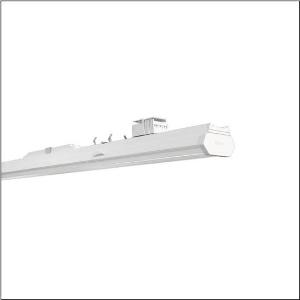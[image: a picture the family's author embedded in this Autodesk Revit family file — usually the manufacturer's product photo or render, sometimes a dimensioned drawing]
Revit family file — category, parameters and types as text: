
# Revit family: licross_21_protected_mo_52td1bvn465g
name_source: partatom
category: Lighting Fixtures
units: mm (PartAtom-declared; Revit-internal decimal feet)

## family parameters
Cut with Voids When Loaded = No
Host = Face
Light Source = No
Part Type = Normal
Room Calculation Point = No
Round Connector Dimension = Use Diameter
Shared = No

## types (1)
- --- (1 x LED, 6500 lm, 39 W, 4000K)
    Apparent Load = 39 VA
    CIE Flux Codes = 54 82 95 97 100
    Color Rendering = 80
    Color Temperature = 4000K
    Default Elevation = 1800 mm
    Description = Licross 21 Protected MO, luminaire insert, of sheet steel, galvanised, coil coated, white, length: 1.500mm, width: 90mm, height: 101mm, LED rated luminous flux: 6.500lm, light colour: 840, SDCM (Standard Deviation of Colour Matching)MacAdam ≤ 3 SDCM (initial), control gear: DALI 2, CLO, with plug, 5-pole, with phase selection, mains connection: 220..240V, AC, 50/60Hz, start of lifetime: 39W, end of service life: 46W, internal wiring halogen-free, primary optical cover: cover, of PMMA, light emission: direct distribution, primary light characteristic: symmetric, protection rating (complete): IP54, insulation class (complete): insulation class I (protective earthing), certification: CE, ENEC, VDE, UKCA, protection symbol: D if used in an environment with non-conductive dust loads with corresponding accessories, impact resistance: IK06, permissible ambient temperature for indoor applications: -25..+45°C, corresponds to IFS (International Featured Standards) requirements for safety and quality in the food industry, reducing of maximum allowable ambient temperature of 5°C with ceiling mounting, LABS conformity tested according to VDMA 24364:2018-05, The light source and the operating device comply with the requirements of the Ecodesign Regulation (EU) 2019/2020 and are replaceable in accordance with this regulation, packaging unit: 1 piece
    Height = 92 mm
    Lamp = 1 x LED
    Lamp Light Flux = 6500 lm
    Lamp Power = 39 W
    Lamp count = 1
    Length = 1500 mm
    Luminous efficacy = 167 lm/W
    Manufacturer = Siteco
    ModVariant = No
    Model = 52TD1BVN465G
    Mounting Place = Ceiling
    Mounting Type = Pendant
    Number of Poles = 1
    OnlyDefault = Yes
    Power Factor = 1
    Product Name = Licross 21 Protected MO
    Product group = luminaire insert | ceiling pendant
    ProductGroupID = 901
    Protection Class = Protection class I
    Protection Degree = IP 54
    RLX_Detail_Level = 1
    RLX_Emergency_Light_Flux = 0 lm
    RLX_Emergency_Type = 0
    RLX_Emergency_Type_DB = No
    RlxData = <blob elided: 24717 chars, md5=7ae968ca>
    Socket = socket
    Standby Power = 0 W
    System Light Flux = 6500 lm
    System Power = 39 W
    Type Comments = factory setting: luminous flux: 100 % | dim-lin: 254 | 262 mA
    Type Image = l_1256148.jpg
    URL = http://relux.com
    VarID = @adj_089423
    Voltage = 0 V
    Weight = 0.00 kg
    Width = 88 mm

## geometry (parser evidence)
native form markers: Blend x4, Sweep x12
no freeform markers — native parametric forms only
